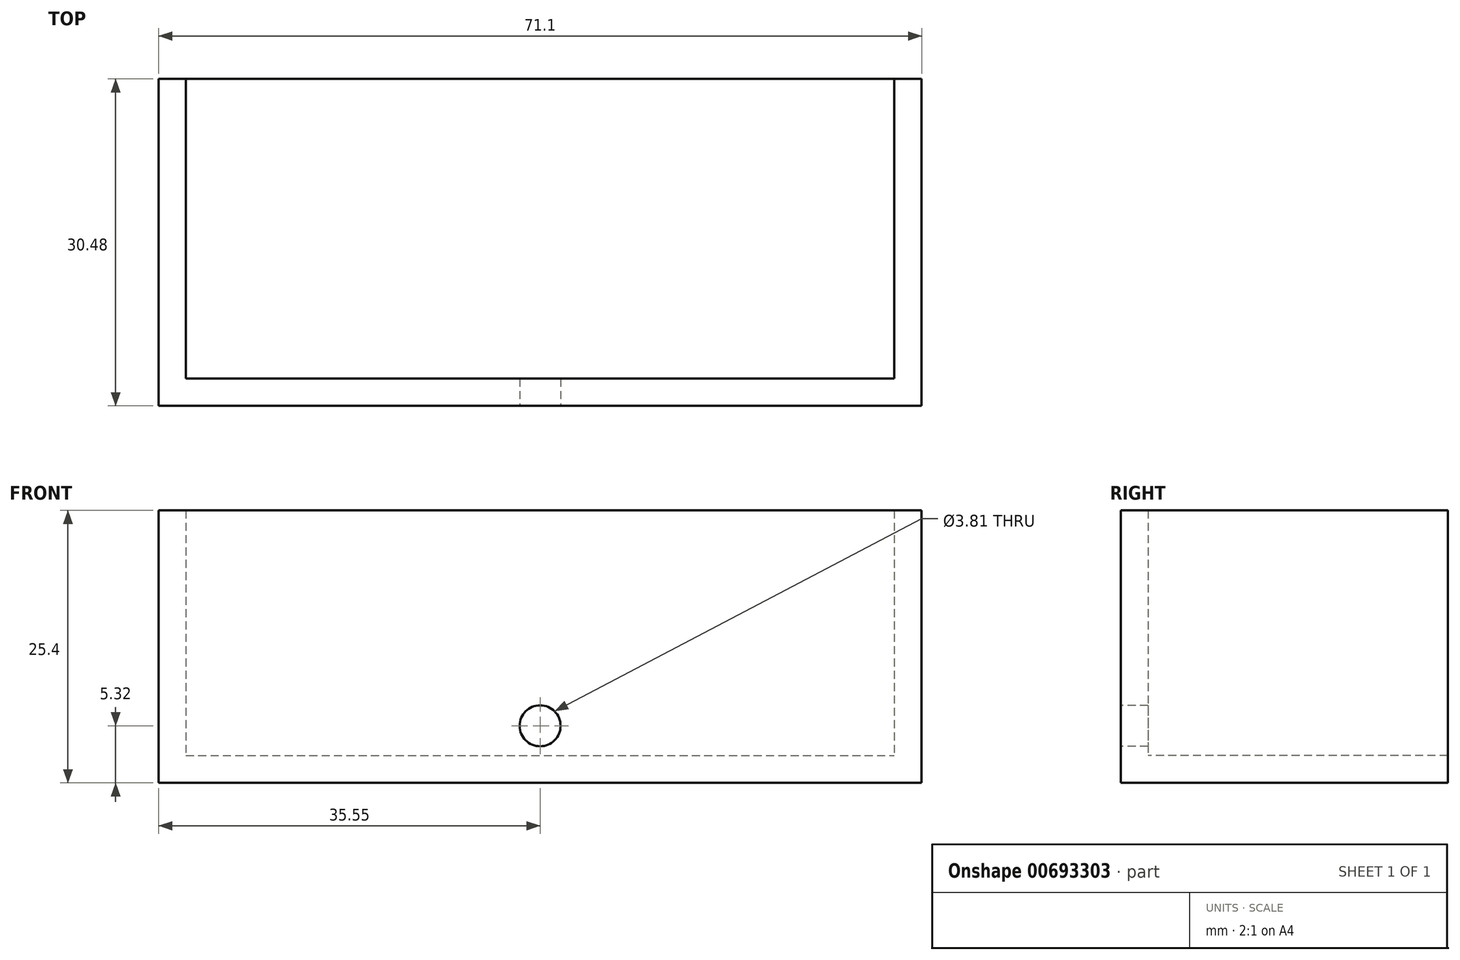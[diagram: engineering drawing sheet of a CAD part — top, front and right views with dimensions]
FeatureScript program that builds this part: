
annotation { "Feature Type Name" : "Feature", "Feature Type Description" : "" }
export const myFeature = defineFeature(function(context is Context, id is Id, definition is map)
    precondition{}
    {
        {
            var Q0;
            Q0=qCreatedBy(makeId("Top.planeOp"),FACE);
            var sketch = newSketch(context, id + "F0", { "sketchPlane" : qUnion([Q0])});
            skLineSegment(sketch, "E0.bottom", {"start": v(-35.55, 15.24) * mm, "end": v(35.55, 15.24) * mm});
            skLineSegment(sketch, "E0.top", {"start": v(-35.55, -15.24) * mm, "end": v(35.55, -15.24) * mm});
            skLineSegment(sketch, "E0.left", {"start": v(-35.55, 15.24) * mm, "end": v(-35.55, -15.24) * mm});
            skLineSegment(sketch, "E0.right", {"start": v(35.55, 15.24) * mm, "end": v(35.55, -15.24) * mm});
            skPoint(sketch, "E0.middle", {"position": v(0, 0) * mm});
            skSolve(sketch);
        }
        {
            var Q0;
            Q0=makeQuery(id+"F0.imprint","IMPRINT",FACE,{"disambiguationData":[TD([[makeQuery(id+"F0.imprint","IMPRINT",EDGE,{"derivedFrom":sQuery(id+"F0.wireOp",EDGE,"E0.bottom")}),-1.0]])]});
            extrude(context, id + "F1", {"entities" : qUnion([Q0]), "depth" : 25.4 * mm, "offsetDistance" : 25.4 * mm});
        }
        {
            var Q0;
            Q0=makeQuery(id+"F1.opExtrude","SWEPT_FACE",FACE,{"disambiguationData":[OSD([sQuery(id+"F0.wireOp",EDGE,"E0.bottom")])]});
            var Q1;
            Q1=makeQuery(id+"F1.opExtrude","CAP_FACE",FACE,{"disambiguationData":[OSD([sQuery(id+"F0.wireOp",EDGE,"E0.bottom"),sQuery(id+"F0.wireOp",EDGE,"E0.top"),sQuery(id+"F0.wireOp",EDGE,"E0.left"),sQuery(id+"F0.wireOp",EDGE,"E0.right")])],"isStart":false});
            shell(context, id + "F2", {"entities" : qUnion([Q0, Q1]), "thickness" : 2.54 * mm});
        }
        {
            var Q0;
            Q0=makeQuery(id+"F1.opExtrude","SWEPT_FACE",FACE,{"disambiguationData":[OSD([sQuery(id+"F0.wireOp",EDGE,"E0.top")])]});
            var sketch = newSketch(context, id + "F3", { "sketchPlane" : qUnion([Q0])});
            skPoint(sketch, "E1", {"position": v(0, 5.32) * mm});
            skSolve(sketch);
        }
        {
            var Q0;
            Q0=sQuery(id+"F3.wireOp",VERTEX,"E1");
            var Q1;
            Q1=makeQuery(id+"F1.opExtrude","SWEPT_BODY",BODY,{"disambiguationData":[OSD([sQuery(id+"F0.wireOp",EDGE,"E0.bottom"),sQuery(id+"F0.wireOp",EDGE,"E0.top"),sQuery(id+"F0.wireOp",EDGE,"E0.left"),sQuery(id+"F0.wireOp",EDGE,"E0.right")])]});
            hole(context, id + "F4", {"style" : HoleStyle.SIMPLE, "endStyle" : HoleEndStyle.THROUGH, "holeDiameter" : 3.8 * mm, "majorDiameter" : 6.35 * mm, "isTappedThrough" : true, "tappedDepth" : 12.7 * mm, "tapClearance" : 3, "locations" : qUnion([Q0]), "scope" : qUnion([Q1])});
        }
    });
